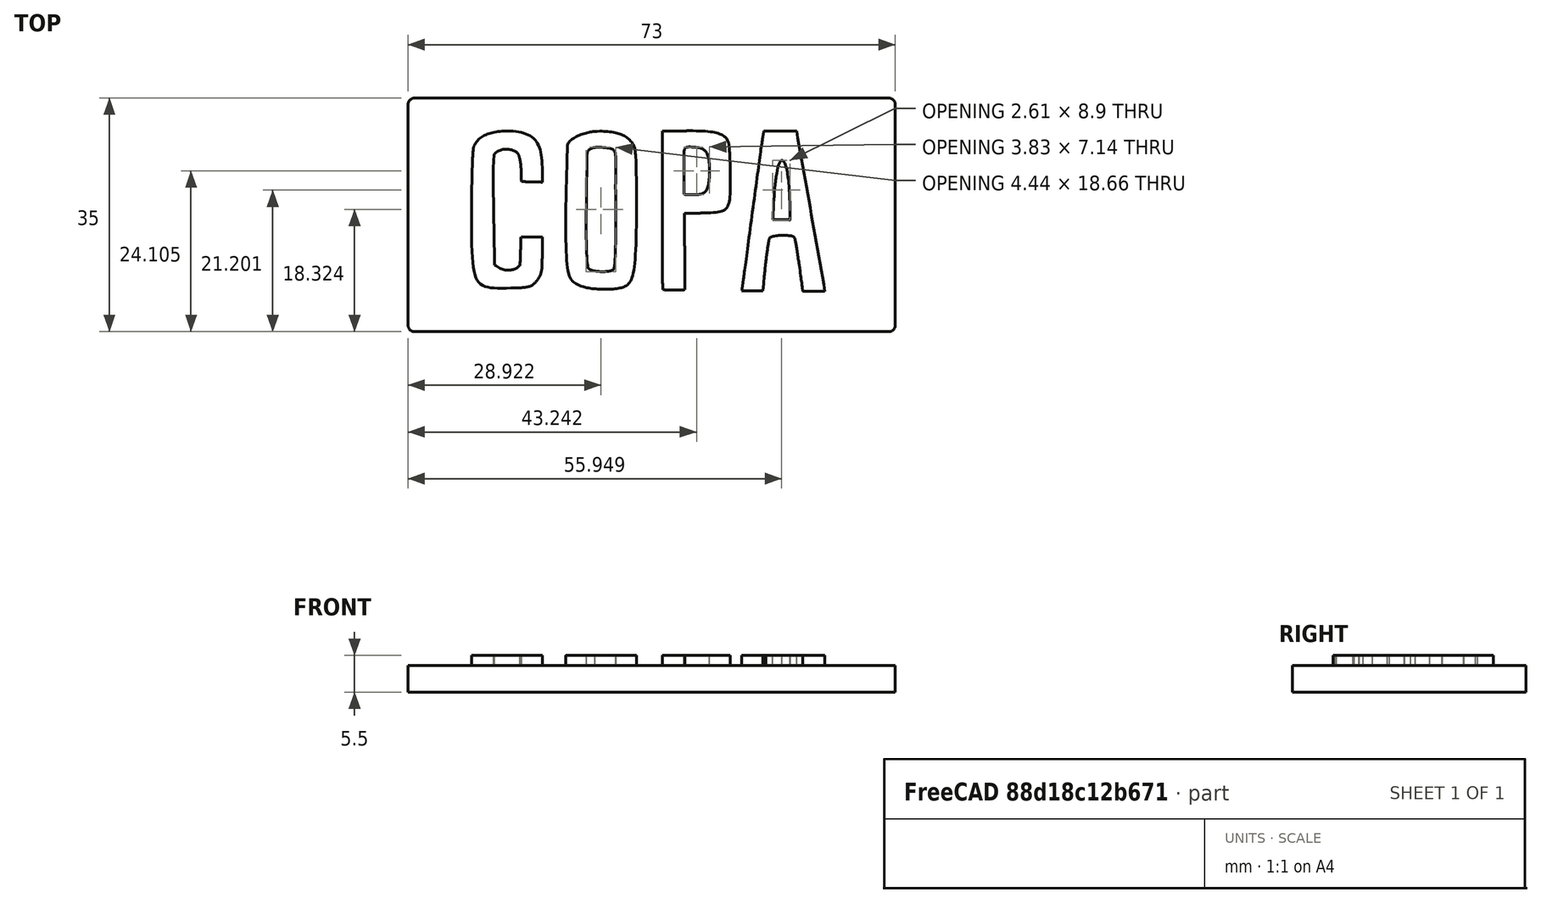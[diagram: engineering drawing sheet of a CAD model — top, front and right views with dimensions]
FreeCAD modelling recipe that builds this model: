
FCSTD DOCUMENT  (FreeCAD 0.16R6712 (Git))
Label: Copa
License: All rights reserved
LicenseURL: http://en.wikipedia.org/wiki/All_rights_reserved
objects: Part::Feature×8, Part::Extrusion×7, Part::Cut×3, Part::Box×1, Part::Fillet×1
note: 20 computed .brp shape members not serialized (recipe doc carries the construction recipe); baked Part::Feature solids carry a one-line shape summary decoded from their .brp

FEATURE [Part::Feature] path4138  label="Rectangulo"
  shape: bbox 73.38 x 33.98 x 2e-07 mm, 0 faces, 0 solids (baked)
FEATURE [Part::Feature] path4138001
  shape: bbox 10.23 x 23.92 x 2e-07 mm, 0 faces, 0 solids (baked)
FEATURE [Part::Feature] path4138002
  shape: bbox 3.831 x 7.194 x 2e-07 mm, 0 faces, 0 solids (baked)
FEATURE [Part::Feature] path4138003
  shape: bbox 12.45 x 24.01 x 2e-07 mm, 0 faces, 0 solids (baked)
FEATURE [Part::Feature] path4138004
  shape: bbox 2.619 x 9.031 x 2e-07 mm, 0 faces, 0 solids (baked)
FEATURE [Part::Feature] path4138005
  shape: bbox 10.6 x 23.67 x 2e-07 mm, 0 faces, 0 solids (baked)
FEATURE [Part::Feature] path4138006
  shape: bbox 10.58 x 23.96 x 2e-07 mm, 0 faces, 0 solids (baked)
FEATURE [Part::Feature] path4138007
  shape: bbox 5.305 x 18.91 x 2e-07 mm, 0 faces, 0 solids (baked)
FEATURE [Part::Box] Box  label="Cube"
  Height = 4
  Length = 73
  Placement = pos=(0,-35,-4) rot=(0,0,1;0rad)
  Width = 35
FEATURE [Part::Extrusion] Extrude
  Base = -> path4138001
  Dir = (0,0,1.5)
  Solid = true
FEATURE [Part::Extrusion] Extrude001
  Base = -> path4138002
  Dir = (0,0,1.5)
  Solid = true
FEATURE [Part::Extrusion] Extrude002
  Base = -> path4138003
  Dir = (0,0,1.5)
  Solid = true
FEATURE [Part::Extrusion] Extrude003
  Base = -> path4138004
  Dir = (0,0,1.5)
  Solid = true
FEATURE [Part::Extrusion] Extrude004
  Base = -> path4138005
  Dir = (0,0,1.5)
  Solid = true
FEATURE [Part::Extrusion] Extrude005
  Base = -> path4138006
  Dir = (0,0,1.5)
  Solid = true
FEATURE [Part::Extrusion] Extrude006
  Base = -> path4138007
  Dir = (0,0,1.5)
  Solid = true
FEATURE [Part::Cut] Cut
  Base = -> Extrude
  Tool = -> Extrude001
FEATURE [Part::Cut] Cut001
  Base = -> Extrude002
  Tool = -> Extrude003
FEATURE [Part::Cut] Cut002
  Base = -> Extrude005
  Tool = -> Extrude006
FEATURE [Part::Fillet] Fillet
  Base = -> Box
  Edges = 4 edges r=1: [Edge1,Edge3,Edge5,Edge7]
